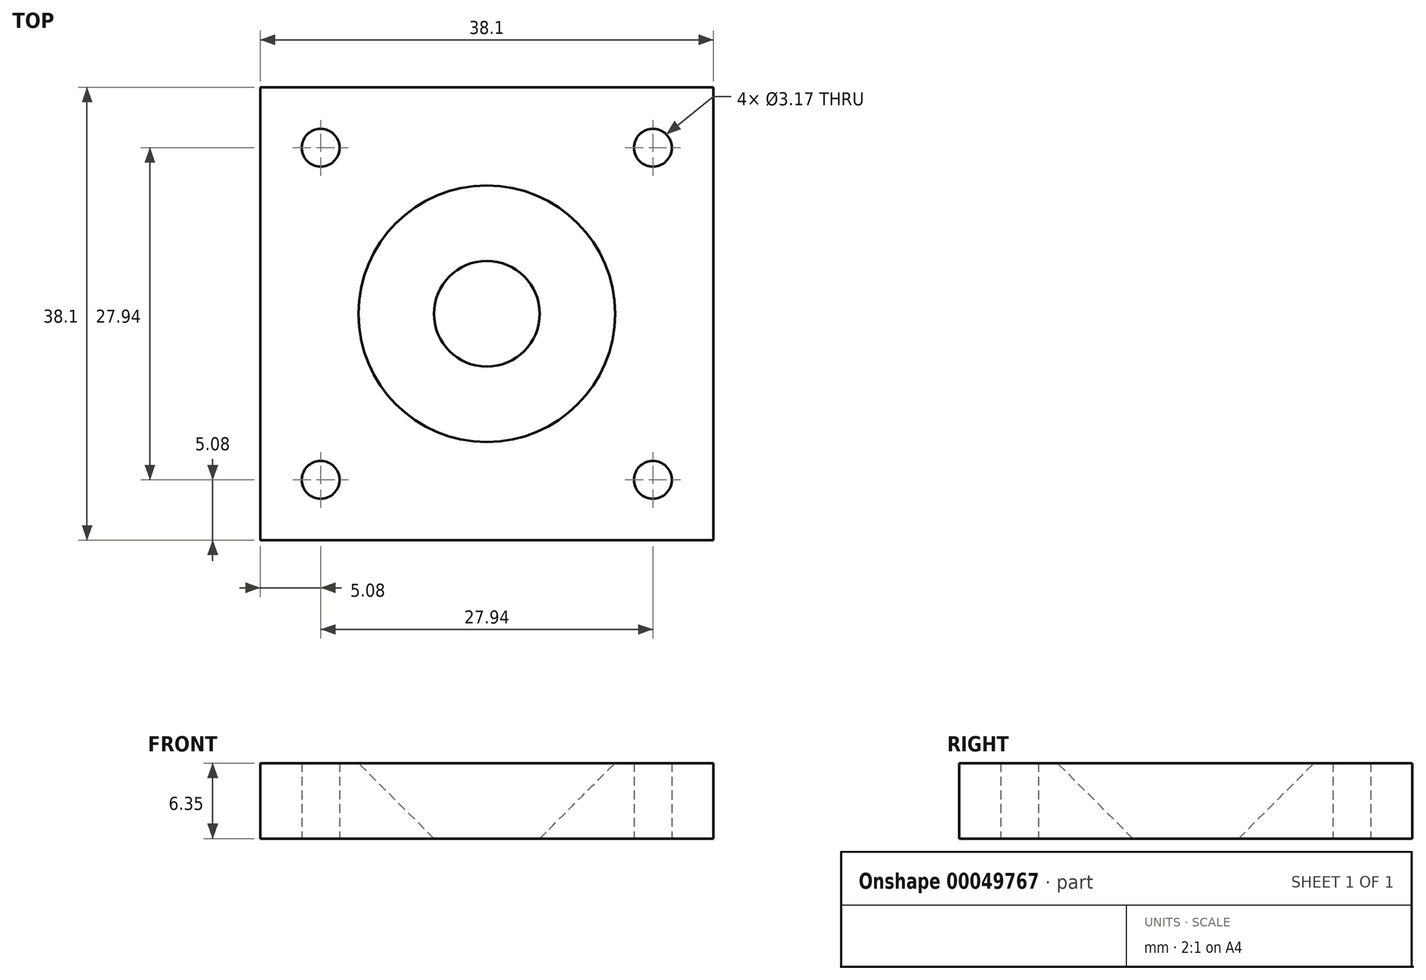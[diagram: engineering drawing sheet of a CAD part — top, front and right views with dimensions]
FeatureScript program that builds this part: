
annotation { "Feature Type Name" : "Feature", "Feature Type Description" : "" }
export const myFeature = defineFeature(function(context is Context, id is Id, definition is map)
    precondition{}
    {
        {
            var Q0;
            Q0=qCreatedBy(makeId("Top.planeOp"),FACE);
            var sketch = newSketch(context, id + "F0", { "sketchPlane" : qUnion([Q0])});
            skLineSegment(sketch, "E0.rect.bottom", {"start": v(19.05, -19.05) * mm, "end": v(-19.05, -19.05) * mm});
            skLineSegment(sketch, "E0.rect.top", {"start": v(19.05, 19.05) * mm, "end": v(-19.05, 19.05) * mm});
            skLineSegment(sketch, "E0.rect.left", {"start": v(19.05, -19.05) * mm, "end": v(19.05, 19.05) * mm});
            skLineSegment(sketch, "E0.rect.right", {"start": v(-19.05, -19.05) * mm, "end": v(-19.05, 19.05) * mm});
            skPoint(sketch, "E0.rect.middle", {"position": v(0, 0) * mm});
            skSolve(sketch);
        }
        {
            var Q0;
            Q0=qSketchRegion(id+"F0",true);
            extrude(context, id + "F1", {"entities" : qUnion([Q0]), "depth" : 6.35 * mm});
        }
        {
            var Q0;
            Q0=qCreatedBy(makeId("Top.planeOp"),FACE);
            var sketch = newSketch(context, id + "F2", { "sketchPlane" : qUnion([Q0])});
            skCircle(sketch, "E1", {"center": v(0, 0) * mm, "radius": 4.45 * mm});
            skSolve(sketch);
        }
        {
            var Q0;
            Q0=qSketchRegion(id+"F2",true);
            extrude(context, id + "F3", {"entities" : qUnion([Q0]), "operationType" : NewBodyOperationType.REMOVE, "depth" : 25.4 * mm});
        }
        {
            var Q0;
            Q0=qSketchRegion(id+"F2",true);
            extrude(context, id + "F4", {"entities" : qUnion([Q0]), "operationType" : NewBodyOperationType.REMOVE, "depth" : 6.35 * mm, "hasDraft" : true, "draftAngle" : 45 * degree});
        }
        {
            var Q0;
            Q0=qCreatedBy(makeId("Top.planeOp"),FACE);
            var sketch = newSketch(context, id + "F5", { "sketchPlane" : qUnion([Q0])});
            skCircle(sketch, "E2", {"center": v(13.97, -13.97) * mm, "radius": 1.59 * mm});
            skCircle(sketch, "E3.MirrorC", {"center": v(13.97, 13.97) * mm, "radius": 1.59 * mm});
            skCircle(sketch, "E4.MirrorC", {"center": v(-13.97, -13.97) * mm, "radius": 1.59 * mm});
            skCircle(sketch, "E5.MirrorC", {"center": v(-13.97, 13.97) * mm, "radius": 1.59 * mm});
            skSolve(sketch);
        }
        {
            var Q0;
            Q0=qSketchRegion(id+"F5",true);
            extrude(context, id + "F6", {"entities" : qUnion([Q0]), "operationType" : NewBodyOperationType.REMOVE, "depth" : 25.4 * mm});
        }
    });
